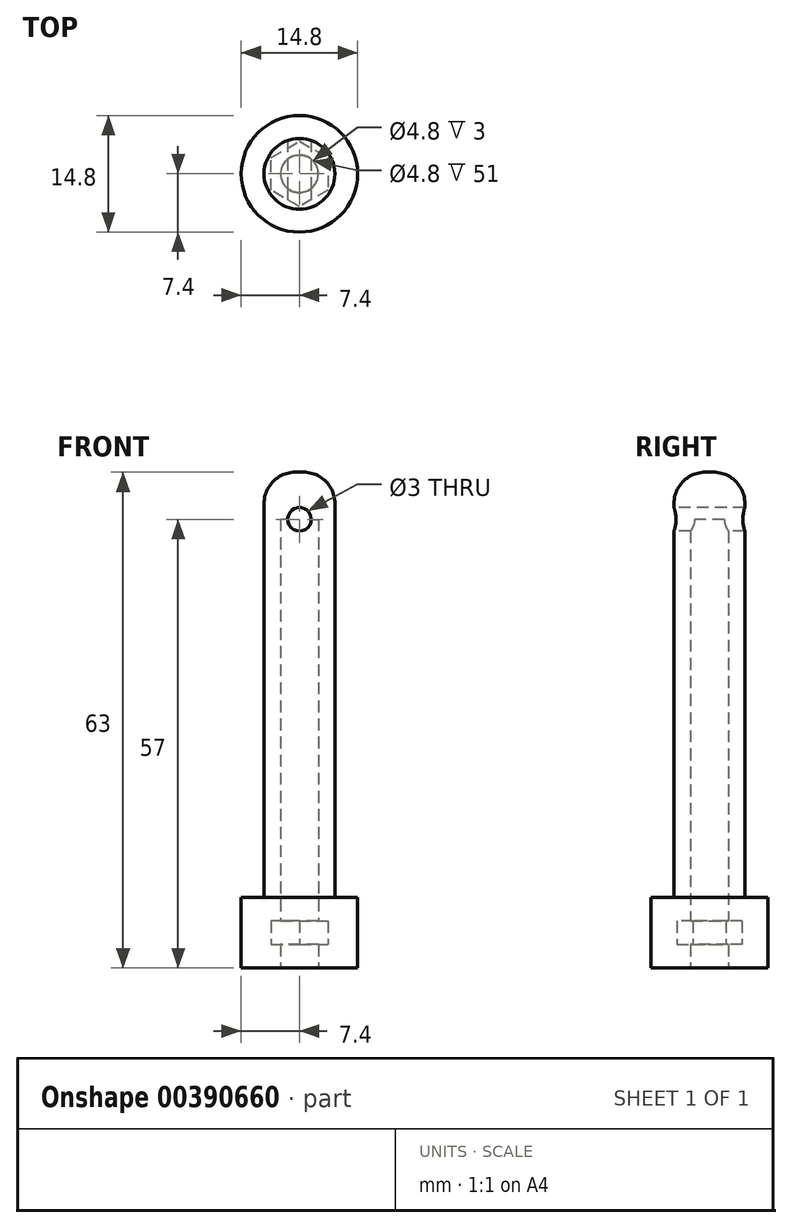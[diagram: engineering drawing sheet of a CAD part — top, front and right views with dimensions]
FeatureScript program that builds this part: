
annotation { "Feature Type Name" : "Feature", "Feature Type Description" : "" }
export const myFeature = defineFeature(function(context is Context, id is Id, definition is map)
    precondition{}
    {
        {
            var Q0;
            Q0=qCreatedBy(makeId("Top.planeOp"),FACE);
            var sketch = newSketch(context, id + "F0", { "sketchPlane" : qUnion([Q0])});
            skCircle(sketch, "E0", {"center": v(0, 0) * mm, "radius": 7.4 * mm});
            skCircle(sketch, "E1", {"center": v(0, 0) * mm, "radius": 2.4 * mm});
            skSolve(sketch);
        }
        {
            var Q0;
            Q0 = qSketchRegion(id + "F0", true);
            extrude(context, id + "F1", {"entities" : qUnion([Q0]), "depth" : 3 * mm, "offsetDistance" : 25 * mm});
        }
        {
            var Q0;
            Q0=makeQuery(id+"F1.opExtrude","CAP_FACE",FACE,{"disambiguationData":[OSD([sQuery(id+"F0.wireOp",EDGE,"E0")])],"isStart":false});
            var sketch = newSketch(context, id + "F2", { "sketchPlane" : qUnion([Q0])});
            skCircle(sketch, "E2.cCircle", {"center": v(0, 0) * mm, "radius": 3.6 * mm, "construction": true});
            skLineSegment(sketch, "E2.0", {"start": v(3.6, 2.08) * mm, "end": v(3.6, -2.08) * mm});
            skLineSegment(sketch, "E2.1", {"start": v(3.6, -2.08) * mm, "end": v(0, -4.16) * mm});
            skLineSegment(sketch, "E2.2", {"start": v(0, -4.16) * mm, "end": v(-3.6, -2.08) * mm});
            skLineSegment(sketch, "E2.3", {"start": v(-3.6, -2.08) * mm, "end": v(-3.6, 2.08) * mm});
            skLineSegment(sketch, "E2.4", {"start": v(-3.6, 2.08) * mm, "end": v(0, 4.16) * mm});
            skLineSegment(sketch, "E2.5", {"start": v(0, 4.16) * mm, "end": v(3.6, 2.08) * mm});
            skPoint(sketch, "E2.0.midPoint", {"position": v(3.6, 0) * mm});
            skSolve(sketch);
        }
        {
            var Q0;
            Q0=makeQuery(id+"F2.imprint","IMPRINT",FACE,{"disambiguationData":[TD([[makeQuery(id+"F2.imprint","IMPRINT",EDGE,{"derivedFrom":sQuery(id+"F2.wireOp",EDGE,"E2.0")}),1.0]])]});
            extrude(context, id + "F3", {"entities" : qUnion([Q0]), "operationType" : NewBodyOperationType.ADD, "depth" : 3 * mm, "offsetDistance" : 25 * mm});
        }
        {
            var Q0;
            Q0=makeQuery(id+"F3.opExtrude","CAP_FACE",FACE,{"disambiguationData":[OSD([sQuery(id+"F0.wireOp",EDGE,"E0"),sQuery(id+"F2.wireOp",EDGE,"E2.0"),sQuery(id+"F2.wireOp",EDGE,"E2.1"),sQuery(id+"F2.wireOp",EDGE,"E2.2"),sQuery(id+"F2.wireOp",EDGE,"E2.3"),sQuery(id+"F2.wireOp",EDGE,"E2.4"),sQuery(id+"F2.wireOp",EDGE,"E2.5")])],"isStart":false});
            var sketch = newSketch(context, id + "F4", { "sketchPlane" : qUnion([Q0])});
            skCircle(sketch, "E3", {"center": v(0, 0) * mm, "radius": 7.4 * mm});
            skCircle(sketch, "E4", {"center": v(0, 0) * mm, "radius": 2.4 * mm});
            skCircle(sketch, "E5", {"center": v(0, 0) * mm, "radius": 4.5 * mm});
            skSolve(sketch);
        }
        {
            var Q0;
            Q0=makeQuery(id+"F4.imprint","IMPRINT",FACE,{"disambiguationData":[TD([[makeQuery(id+"F4.imprint","IMPRINT",EDGE,{"derivedFrom":sQuery(id+"F4.wireOp",EDGE,"E4")}),-1.0]])]});
            var Q1;
            Q1=makeQuery(id+"F4.imprint","IMPRINT",FACE,{"disambiguationData":[TD([[makeQuery(id+"F4.imprint","IMPRINT",EDGE,{"derivedFrom":sQuery(id+"F4.wireOp",EDGE,"E5")}),1.0]])]});
            extrude(context, id + "F5", {"entities" : qUnion([Q0, Q1]), "operationType" : NewBodyOperationType.ADD, "depth" : 51 * mm, "offsetDistance" : 25 * mm});
        }
        {
            var Q0;
            Q0=makeQuery(id+"F3.opExtrude","CAP_FACE",FACE,{"disambiguationData":[OSD([sQuery(id+"F0.wireOp",EDGE,"E0"),sQuery(id+"F2.wireOp",EDGE,"E2.0"),sQuery(id+"F2.wireOp",EDGE,"E2.1"),sQuery(id+"F2.wireOp",EDGE,"E2.2"),sQuery(id+"F2.wireOp",EDGE,"E2.3"),sQuery(id+"F2.wireOp",EDGE,"E2.4"),sQuery(id+"F2.wireOp",EDGE,"E2.5")])],"isStart":false});
            extrude(context, id + "F6", {"entities" : qUnion([Q0]), "operationType" : NewBodyOperationType.ADD, "depth" : 3 * mm, "offsetDistance" : 25 * mm});
        }
        {
            var Q0;
            Q0=makeQuery(id+"F5.opExtrude","CAP_FACE",FACE,{"disambiguationData":[OSD([sQuery(id+"F4.wireOp",EDGE,"E4"),sQuery(id+"F4.wireOp",EDGE,"E5")])],"isStart":false});
            var sketch = newSketch(context, id + "F7", { "sketchPlane" : qUnion([Q0])});
            skCircle(sketch, "E6", {"center": v(0, 0) * mm, "radius": 4.5 * mm});
            skSolve(sketch);
        }
        {
            var Q0;
            Q0 = qSketchRegion(id + "F7", true);
            extrude(context, id + "F8", {"entities" : qUnion([Q0]), "operationType" : NewBodyOperationType.ADD, "depth" : 6 * mm, "offsetDistance" : 25 * mm});
        }
        {
            var Q0;
            Q0=makeQuery(id+"F6.opExtrude","CAP_EDGE",EDGE,{"disambiguationData":[OSD([sQuery(id+"F4.wireOp",EDGE,"E5")])],"isStart":false});
            var Q1;
            Q1=makeQuery(id+"F8.opExtrude","CAP_EDGE",EDGE,{"disambiguationData":[OSD([sQuery(id+"F7.wireOp",EDGE,"E6")])],"isStart":false});
            fillet(context, id + "F9", {"entities" : qUnion([Q0, Q1]), "radius" : 4 * mm, "tangentPropagation" : true, "allowEdgeOverflow" : false});
        }
        {
            var Q0;
            Q0=qCreatedBy(makeId("Front.planeOp"),FACE);
            var sketch = newSketch(context, id + "F10", { "sketchPlane" : qUnion([Q0])});
            skCircle(sketch, "E7", {"center": v(0, 57) * mm, "radius": 1.5 * mm});
            skSolve(sketch);
        }
        {
            var Q0;
            Q0 = qSketchRegion(id + "F10", true);
            extrude(context, id + "F11", {"entities" : qUnion([Q0]), "operationType" : NewBodyOperationType.REMOVE, "oppositeDirection" : true, "depth" : 25 * mm, "offsetDistance" : 25 * mm, "symmetric" : true});
        }
    });
